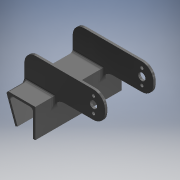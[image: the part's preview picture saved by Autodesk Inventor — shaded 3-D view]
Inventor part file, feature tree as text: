
AUTODESK INVENTOR PART (.ipt)
format: ipt  version: 2019 (Build 230136000, 136)  size: 211,456 bytes
history: native  units: mm (DEFAULTED — no unit token found)
features: sketch x5, extrude x3, fillet x2, hole x2, projected_geometry x1
ambient origin geometry x8: Origin, YZ Plane, XZ Plane, XY Plane, X Axis, Y Axis, Z Axis, Center Point
bodies: Solid1 (feature_tree)
feature tree (13):
  extrude  "Extrusion1"  Depth=95.25mm
  extrude  "Extrusion3"  Depth=50.8mm
  extrude  "Extrusion6"  Depth=2.54mm
  fillet  "Fillet5"  Radius=22.225mm
  fillet  "Fillet6"  Radius=95.25mm
  hole  "Hole1"  [1 undecoded]
  hole  "Hole2"  [1 undecoded]
  sketch  "Sketch1"  dims[d0=31.75mm d1=95.25mm]
  sketch  "Sketch3"  dims[d2=2.54mm d3=0.0mm d8=50.8mm]
  sketch  "Sketch4"  dims[d9=2.54mm d10=2.54mm d11=22.225mm d12=95.25mm]
  projected_geometry  "Projected Loop1"
  sketch  "Sketch5"  dims[d13=57.15mm d14=2.54mm]
  sketch  "Sketch6"  dims[d15=2.54mm d16=57.15mm d17=29.21mm d18=0.0mm d23=2.54mm d24=29.21mm d29=2.54mm d30=3.490659mm d31=28.575mm d32=95.25mm d33=0.0mm d34=12.7mm d35=3.175mm d36=29.21mm d37=12.7mm d38=14.605mm d39=8.0772mm d40=7.5mm d41=3.75mm d42=2.5mm d43=90.0deg d44=10.0mm d45=20.594885mm d46=16.764mm d47=0.0mm d48=0.0mm d49=3.4798mm d50=7.5mm d51=3.75mm d52=2.5mm d53=90.0deg d54=10.0mm d55=20.594885mm]
note: 2 required parameter values undecoded (feature->parameter linkage not recoverable at this tier; creation-order binding heuristic only, values carry confidence <= 0.55)
